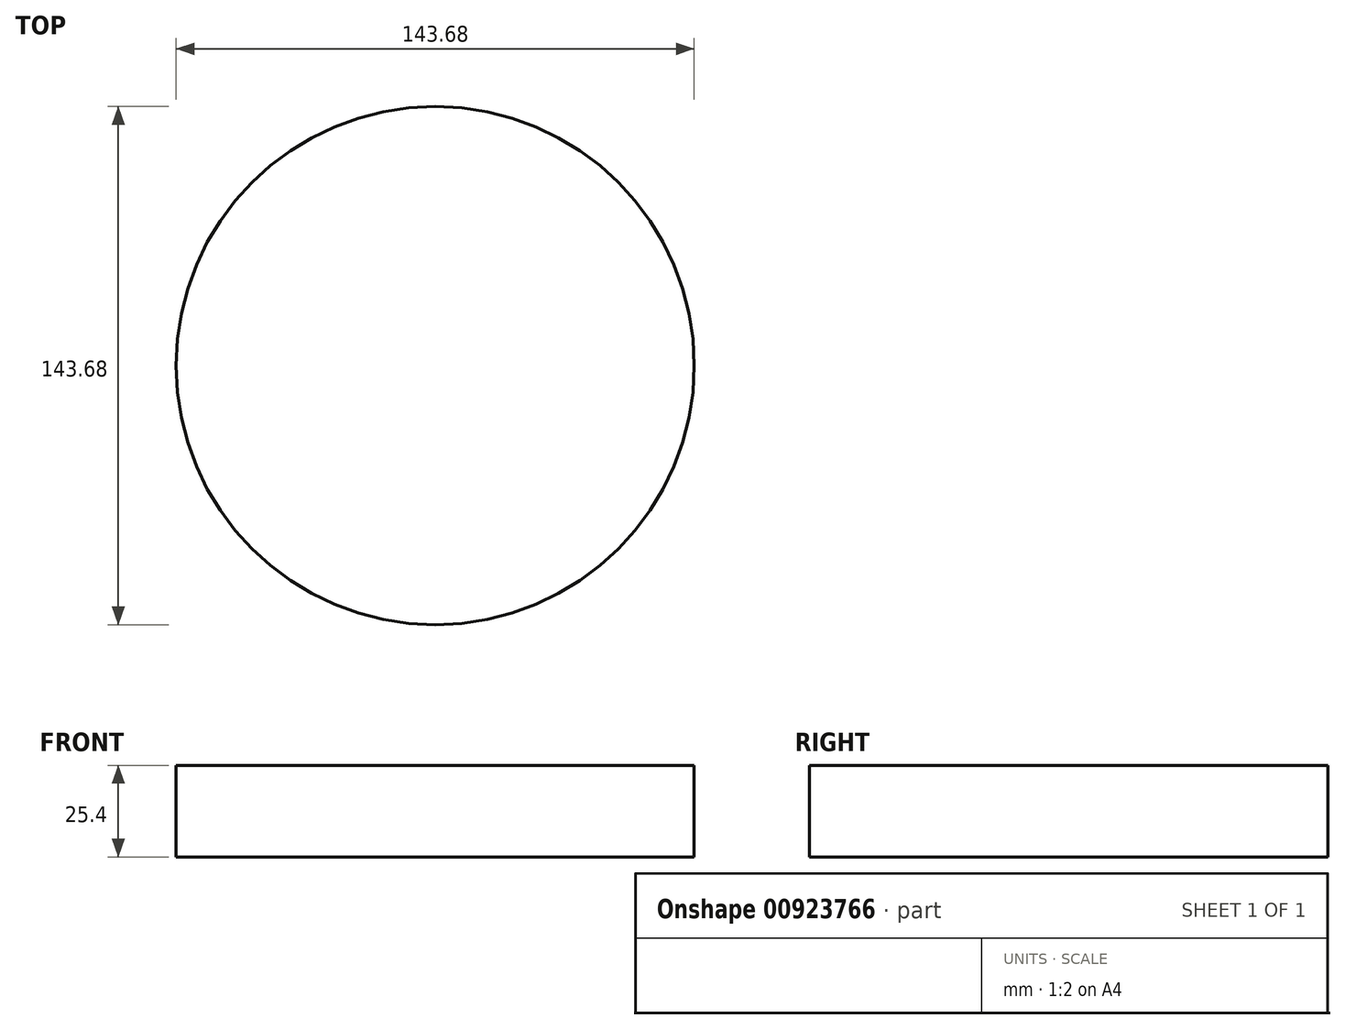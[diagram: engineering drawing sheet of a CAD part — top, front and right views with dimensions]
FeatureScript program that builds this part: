
annotation { "Feature Type Name" : "Feature", "Feature Type Description" : "" }
export const myFeature = defineFeature(function(context is Context, id is Id, definition is map)
    precondition{}
    {
        {
            var Q0;
            Q0=qCreatedBy(makeId("Top.planeOp"),FACE);
            var sketch = newSketch(context, id + "F0", { "sketchPlane" : qUnion([Q0])});
            skCircle(sketch, "E0", {"center": v(0, 0) * mm, "radius": 68.46 * mm});
            skCircle(sketch, "E1", {"center": v(0, 0) * mm, "radius": 58.68 * mm});
            skSolve(sketch);
        }
        {
            var Q0;
            Q0=sQuery(id+"F0.wireOp",EDGE,"E0");
            var Q1;
            Q1=sQuery(id+"F0.wireOp",EDGE,"E1");
            extrude(context, id + "F1", {"bodyType" : ToolBodyType.SURFACE, "surfaceEntities" : qUnion([Q0, Q1]), "depth" : 150 * mm, "offsetDistance" : 25.4 * mm});
        }
        {
            var Q0;
            Q0=qCreatedBy(makeId("Top.planeOp"),FACE);
            var sketch = newSketch(context, id + "F2", { "sketchPlane" : qUnion([Q0])});
            skCircle(sketch, "E2", {"center": v(0, 0) * mm, "radius": 71.84 * mm});
            skSolve(sketch);
        }
        {
            var Q0;
            Q0=makeQuery(id+"F2.imprint","IMPRINT",FACE,{"disambiguationData":[TD([[makeQuery(id+"F2.imprint","IMPRINT",EDGE,{"derivedFrom":sQuery(id+"F2.wireOp",EDGE,"E2")}),1.0]])]});
            extrude(context, id + "F3", {"entities" : qUnion([Q0]), "depth" : 25.4 * mm, "offsetDistance" : 25.4 * mm});
        }
    });
